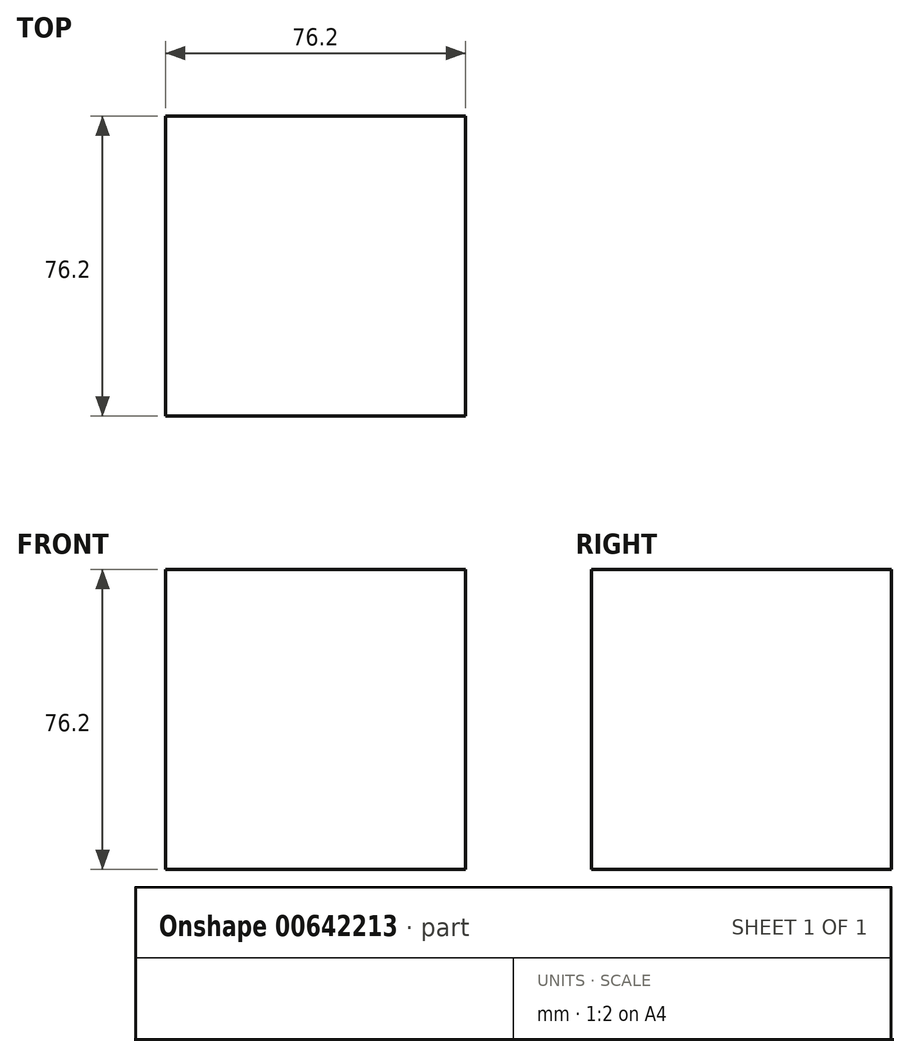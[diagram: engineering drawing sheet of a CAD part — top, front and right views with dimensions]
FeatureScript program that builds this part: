
annotation { "Feature Type Name" : "Feature", "Feature Type Description" : "" }
export const myFeature = defineFeature(function(context is Context, id is Id, definition is map)
    precondition{}
    {
        {
            var Q0;
            Q0=qCreatedBy(makeId("Front.planeOp"),FACE);
            var sketch = newSketch(context, id + "F0", { "sketchPlane" : qUnion([Q0])});
            skLineSegment(sketch, "E0.bottom", {"start": v(-45.37, 86.16) * mm, "end": v(30.83, 86.16) * mm});
            skLineSegment(sketch, "E0.top", {"start": v(-45.37, 9.96) * mm, "end": v(30.83, 9.96) * mm});
            skLineSegment(sketch, "E0.left", {"start": v(-45.37, 86.16) * mm, "end": v(-45.37, 9.96) * mm});
            skLineSegment(sketch, "E0.right", {"start": v(30.83, 86.16) * mm, "end": v(30.83, 9.96) * mm});
            skSolve(sketch);
        }
        {
            var Q0;
            Q0 = qSketchRegion(id + "F0", true);
            extrude(context, id + "F1", {"entities" : qUnion([Q0]), "depth" : 76.2 * mm, "offsetDistance" : 25.4 * mm});
        }
    });
